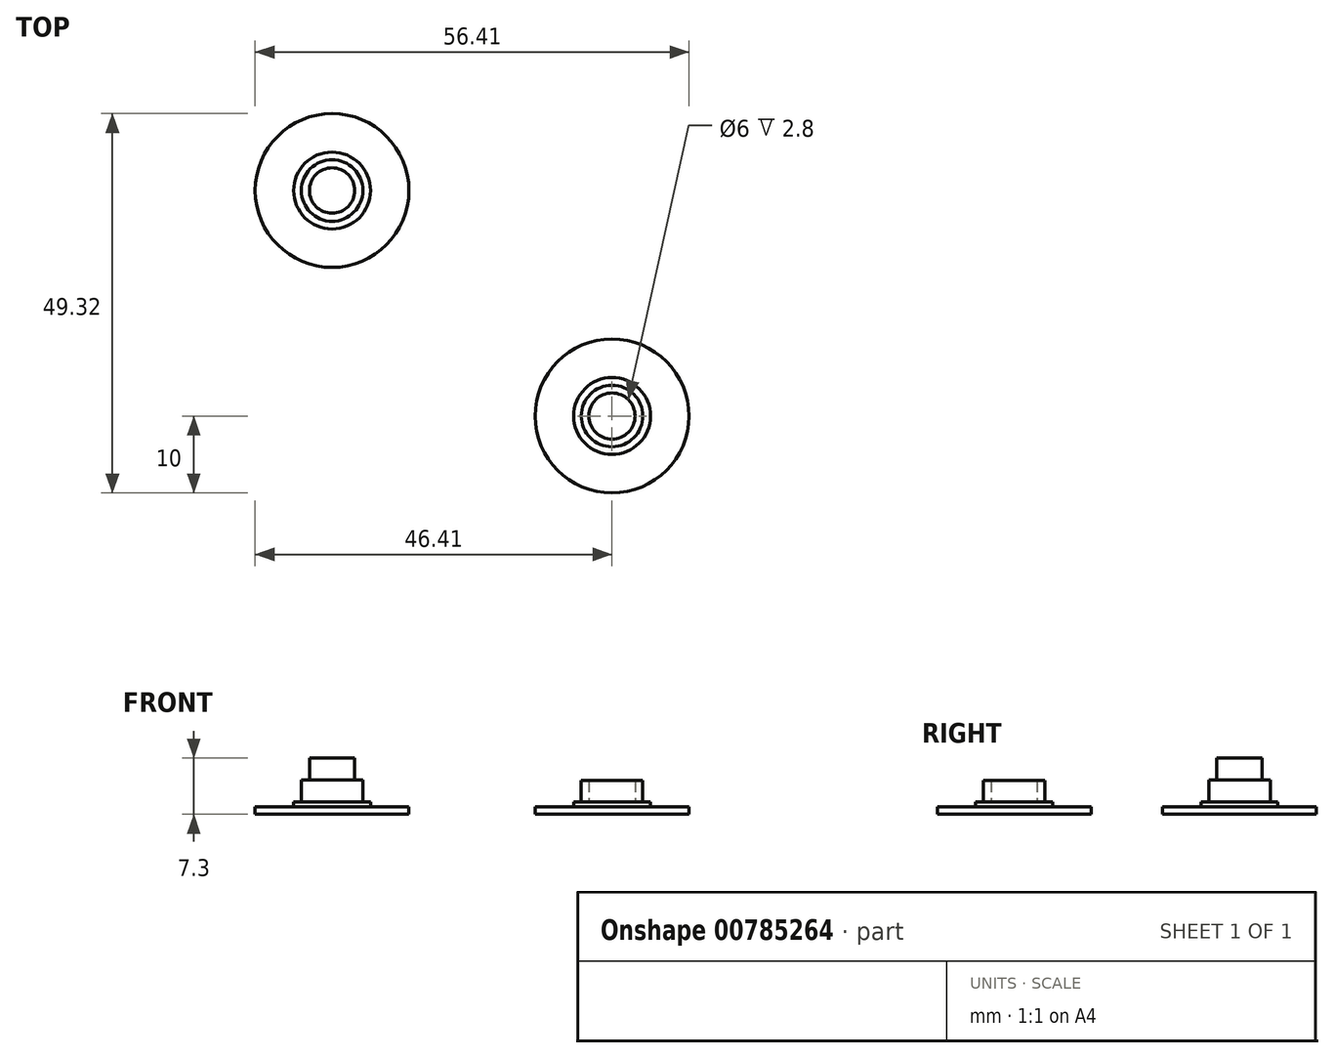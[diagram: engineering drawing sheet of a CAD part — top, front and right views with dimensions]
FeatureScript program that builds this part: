
annotation { "Feature Type Name" : "Feature", "Feature Type Description" : "" }
export const myFeature = defineFeature(function(context is Context, id is Id, definition is map)
    precondition{}
    {
        {
            var Q0;
            Q0=qCreatedBy(makeId("Top.planeOp"),FACE);
            var sketch = newSketch(context, id + "F0", { "sketchPlane" : qUnion([Q0])});
            skCircle(sketch, "E0", {"center": v(0, 0) * mm, "radius": 10 * mm});
            skSolve(sketch);
        }
        {
            var Q0;
            Q0=makeQuery(id+"F0.imprint","IMPRINT",FACE,{"disambiguationData":[TD([[makeQuery(id+"F0.imprint","IMPRINT",EDGE,{"derivedFrom":sQuery(id+"F0.wireOp",EDGE,"E0")}),1.0]])]});
            extrude(context, id + "F1", {"entities" : qUnion([Q0]), "depth" : 1 * mm, "offsetDistance" : 25 * mm});
        }
        {
            var Q0;
            Q0=makeQuery(id+"F1.opExtrude","CAP_FACE",FACE,{"disambiguationData":[OSD([sQuery(id+"F0.wireOp",EDGE,"E0")])],"isStart":false});
            var sketch = newSketch(context, id + "F2", { "sketchPlane" : qUnion([Q0])});
            skCircle(sketch, "E1", {"center": v(0, 0) * mm, "radius": 4 * mm});
            skSolve(sketch);
        }
        {
            var Q0;
            Q0=makeQuery(id+"F2.imprint","IMPRINT",FACE,{"disambiguationData":[TD([[makeQuery(id+"F2.imprint","IMPRINT",EDGE,{"derivedFrom":sQuery(id+"F2.wireOp",EDGE,"E1")}),1.0]])]});
            extrude(context, id + "F3", {"entities" : qUnion([Q0]), "operationType" : NewBodyOperationType.ADD, "depth" : 3.4 * mm, "offsetDistance" : 25 * mm});
        }
        {
            var Q0;
            Q0=makeQuery(id+"F3.opExtrude","CAP_FACE",FACE,{"disambiguationData":[OSD([sQuery(id+"F2.wireOp",EDGE,"E1")])],"isStart":false});
            shell(context, id + "F4", {"entities" : qUnion([Q0]), "thickness" : 1 * mm});
        }
        {
            var Q0;
            Q0=makeQuery(id+"F1.opExtrude","CAP_FACE",FACE,{"disambiguationData":[OSD([sQuery(id+"F0.wireOp",EDGE,"E0")])],"isStart":false});
            var sketch = newSketch(context, id + "F5", { "sketchPlane" : qUnion([Q0])});
            skCircle(sketch, "E2", {"center": v(0, 0) * mm, "radius": 5 * mm});
            skSolve(sketch);
        }
        {
            var Q0;
            Q0 = qSketchRegion(id + "F5", true);
            extrude(context, id + "F6", {"entities" : qUnion([Q0]), "operationType" : NewBodyOperationType.ADD, "depth" : .6 * mm, "offsetDistance" : 25 * mm});
        }
        {
            var Q0;
            Q0=qCreatedBy(makeId("Top.planeOp"),FACE);
            var sketch = newSketch(context, id + "F7", { "sketchPlane" : qUnion([Q0])});
            skCircle(sketch, "E3", {"center": v(-36.41, 29.32) * mm, "radius": 10 * mm});
            skSolve(sketch);
        }
        {
            var Q0;
            Q0=makeQuery(id+"F7.imprint","IMPRINT",FACE,{"disambiguationData":[TD([[makeQuery(id+"F7.imprint","IMPRINT",EDGE,{"derivedFrom":sQuery(id+"F7.wireOp",EDGE,"E3")}),1.0]])]});
            extrude(context, id + "F8", {"entities" : qUnion([Q0]), "depth" : 1 * mm, "offsetDistance" : 25 * mm});
        }
        {
            var Q0;
            Q0=makeQuery(id+"F8.opExtrude","CAP_FACE",FACE,{"disambiguationData":[OSD([sQuery(id+"F7.wireOp",EDGE,"E3")])],"isStart":false});
            var sketch = newSketch(context, id + "F9", { "sketchPlane" : qUnion([Q0])});
            skCircle(sketch, "E4", {"center": v(-36.41, 29.32) * mm, "radius": 4 * mm});
            skSolve(sketch);
        }
        {
            var Q0;
            Q0=makeQuery(id+"F9.imprint","IMPRINT",FACE,{"disambiguationData":[TD([[makeQuery(id+"F9.imprint","IMPRINT",EDGE,{"derivedFrom":sQuery(id+"F9.wireOp",EDGE,"E4")}),1.0]])]});
            extrude(context, id + "F10", {"entities" : qUnion([Q0]), "operationType" : NewBodyOperationType.ADD, "depth" : 3.5 * mm, "offsetDistance" : 25 * mm});
        }
        {
            var Q0;
            Q0=makeQuery(id+"F10.opExtrude","CAP_FACE",FACE,{"disambiguationData":[OSD([sQuery(id+"F9.wireOp",EDGE,"E4")])],"isStart":false});
            var sketch = newSketch(context, id + "F11", { "sketchPlane" : qUnion([Q0])});
            skCircle(sketch, "E5", {"center": v(-36.41, 29.32) * mm, "radius": 2.95 * mm});
            skSolve(sketch);
        }
        {
            var Q0;
            Q0 = qSketchRegion(id + "F11", true);
            extrude(context, id + "F12", {"entities" : qUnion([Q0]), "operationType" : NewBodyOperationType.ADD, "depth" : 2.8 * mm, "offsetDistance" : 25 * mm});
        }
        {
            var Q0;
            Q0=makeQuery(id+"F8.opExtrude","CAP_FACE",FACE,{"disambiguationData":[OSD([sQuery(id+"F7.wireOp",EDGE,"E3")])],"isStart":false});
            var sketch = newSketch(context, id + "F13", { "sketchPlane" : qUnion([Q0])});
            skCircle(sketch, "E6", {"center": v(-36.41, 29.32) * mm, "radius": 5 * mm});
            skSolve(sketch);
        }
        {
            var Q0;
            Q0=makeQuery(id+"F13.imprint","IMPRINT",FACE,{"disambiguationData":[TD([[makeQuery(id+"F13.imprint","IMPRINT",EDGE,{"derivedFrom":sQuery(id+"F13.wireOp",EDGE,"E6")}),1.0]])]});
            extrude(context, id + "F14", {"entities" : qUnion([Q0]), "operationType" : NewBodyOperationType.ADD, "depth" : .6 * mm, "offsetDistance" : 25 * mm});
        }
    });
